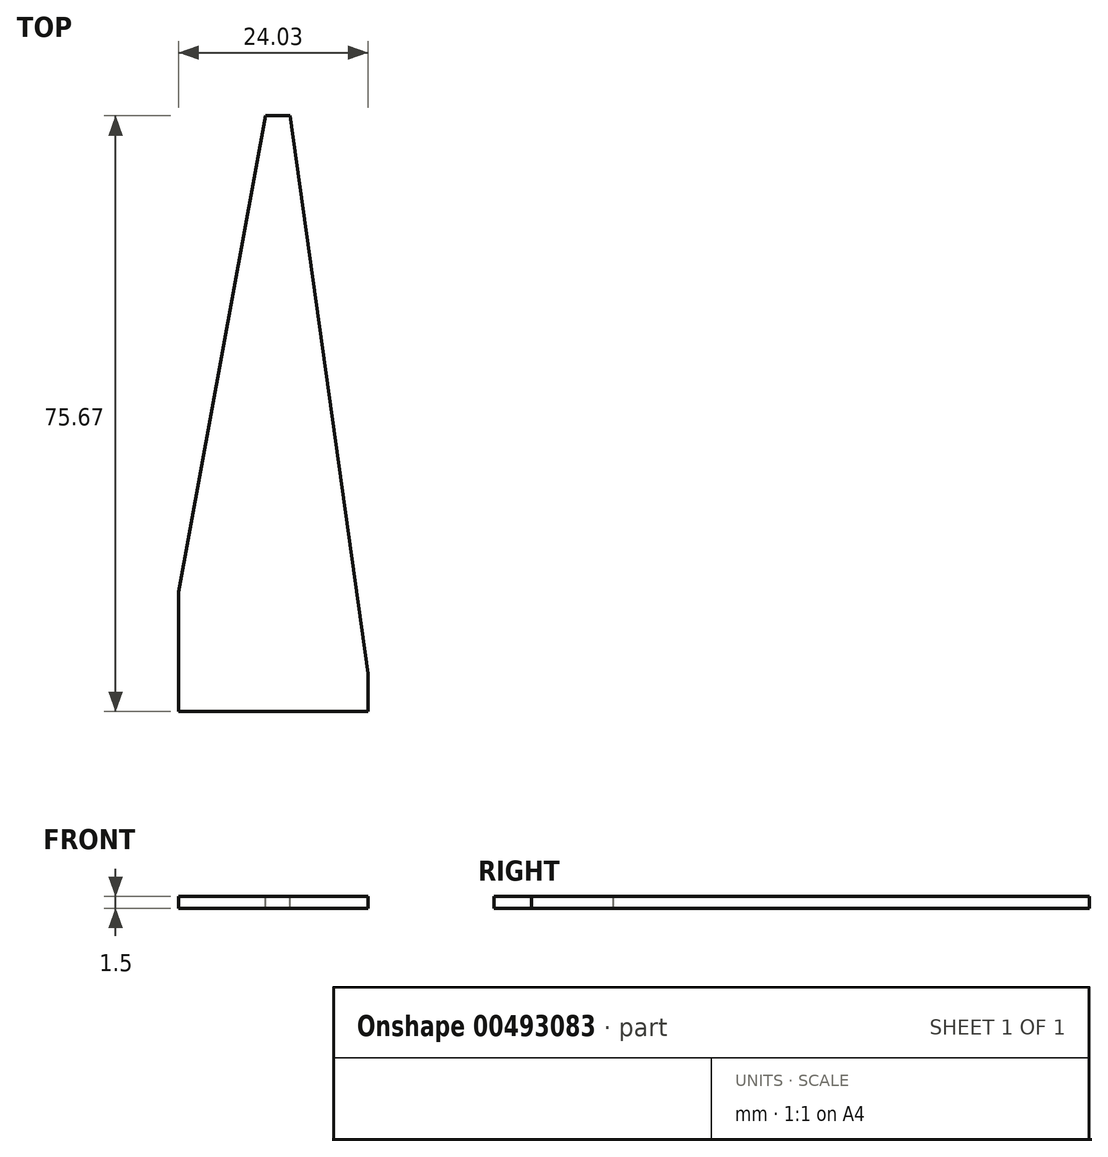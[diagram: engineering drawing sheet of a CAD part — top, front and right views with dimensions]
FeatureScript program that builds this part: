
annotation { "Feature Type Name" : "Feature", "Feature Type Description" : "" }
export const myFeature = defineFeature(function(context is Context, id is Id, definition is map)
    precondition{}
    {
        {
            var Q0;
            Q0=qCreatedBy(makeId("Top.planeOp"),FACE);
            var sketch = newSketch(context, id + "F0", { "sketchPlane" : qUnion([Q0])});
            skLineSegment(sketch, "E0.bottom", {"start": v(-24.03, -54.1) * mm, "end": v(0, -54.1) * mm});
            skLineSegment(sketch, "E0.top", {"start": v(-24.03, 21.57) * mm, "end": v(0, 21.57) * mm});
            skLineSegment(sketch, "E0.left", {"start": v(-24.03, -54.1) * mm, "end": v(-24.03, 21.57) * mm});
            skLineSegment(sketch, "E0.right", {"start": v(0, -54.1) * mm, "end": v(0, 21.57) * mm});
            skSolve(sketch);
        }
        {
            var Q0;
            Q0=makeQuery(id+"F0.imprint","IMPRINT",FACE,{"disambiguationData":[TD([[makeQuery(id+"F0.imprint","IMPRINT",EDGE,{"derivedFrom":sQuery(id+"F0.wireOp",EDGE,"E0.bottom")}),1.0]])]});
            var sketch = newSketch(context, id + "F1", { "sketchPlane" : qUnion([Q0])});
            skLineSegment(sketch, "E1", {"start": v(-25.91, -49.3) * mm, "end": v(-12.05, 26.9) * mm});
            skLineSegment(sketch, "E2", {"start": v(-12.05, 26.9) * mm, "end": v(-37.44, 26.9) * mm});
            skLineSegment(sketch, "E3", {"start": v(-37.44, 26.9) * mm, "end": v(-25.91, -49.3) * mm});
            skLineSegment(sketch, "E4", {"start": v(0, -49.3) * mm, "end": v(-10.6, 26.9) * mm});
            skLineSegment(sketch, "E5", {"start": v(-10.6, 26.9) * mm, "end": v(15.55, 26.9) * mm});
            skLineSegment(sketch, "E6", {"start": v(15.55, 26.9) * mm, "end": v(0, -49.3) * mm});
            skSolve(sketch);
        }
        {
            var Q0;
            Q0 = qSketchRegion(id + "F0", true);
            extrude(context, id + "F2", {"entities" : qUnion([Q0]), "depth" : 1.5 * mm});
        }
        {
            var Q0;
            Q0 = qSketchRegion(id + "F1", true);
            extrude(context, id + "F3", {"entities" : qUnion([Q0]), "operationType" : NewBodyOperationType.REMOVE, "depth" : 2 * mm});
        }
    });
